FCSTD DOCUMENT  (FreeCAD 0.14R2935 (Git))
Label: C-beam gantry plate
License: CC-BY 3.0
LicenseURL: http://creativecommons.org/licenses/by/3.0/
objects: Mesh::Feature×1, Sketcher::SketchObject×1
note: 1 computed .brp shape members not serialized (recipe doc carries the construction recipe); baked Part::Feature solids carry a one-line shape summary decoded from their .brp

FEATURE [Mesh::Feature] C_Beam_Gantry_Plate_V1_STL  label="C-Beam_Gantry Plate_V1_STL"
FEATURE [Sketcher::SketchObject] Sketch
  Placement = pos=(77.6,0,0) rot=(0,0,1;1.5708rad)
  sketch-geometry (18):
    g0: LineSegment StartX=0 StartY=0 StartZ=0 EndX=77.51 EndY=0 EndZ=0
    g1: LineSegment StartX=77.51 StartY=0 StartZ=0 EndX=77.51 EndY=77.51 EndZ=0
    g2: LineSegment StartX=77.51 StartY=77.51 StartZ=0 EndX=0 EndY=77.51 EndZ=0
    g3: LineSegment StartX=0 StartY=77.51 StartZ=0 EndX=0 EndY=0 EndZ=0
    g4: Circle CenterX=8.75 CenterY=68.76 CenterZ=0 NormalX=0 NormalY=0 NormalZ=1 Radius=2.55
    g5: Circle CenterX=8.76 CenterY=38.76 CenterZ=0 NormalX=0 NormalY=0 NormalZ=1 Radius=2.55
    g6: Circle CenterX=8.76 CenterY=8.76 CenterZ=0 NormalX=0 NormalY=0 NormalZ=1 Radius=2.55
    g7: Circle CenterX=28.75 CenterY=68.75 CenterZ=0 NormalX=0 NormalY=0 NormalZ=1 Radius=2.55
    g8: Circle CenterX=48.75 CenterY=68.75 CenterZ=0 NormalX=0 NormalY=0 NormalZ=1 Radius=2.55
    g9: Circle CenterX=68.75 CenterY=68.75 CenterZ=0 NormalX=0 NormalY=0 NormalZ=1 Radius=2.55
    g10: Circle CenterX=68.75 CenterY=8.76 CenterZ=0 NormalX=0 NormalY=0 NormalZ=1 Radius=2.55
    g11: Circle CenterX=48.76 CenterY=8.76 CenterZ=0 NormalX=0 NormalY=0 NormalZ=1 Radius=2.55
    g12: Circle CenterX=28.76 CenterY=8.76 CenterZ=0 NormalX=0 NormalY=0 NormalZ=1 Radius=2.55
    g13: Circle CenterX=68.75 CenterY=38.76 CenterZ=0 NormalX=0 NormalY=0 NormalZ=1 Radius=2.55
    g14: Circle CenterX=18.755 CenterY=58.7909 CenterZ=0 NormalX=0 NormalY=0 NormalZ=1 Radius=2.55
    g15: Circle CenterX=58.755 CenterY=58.7765 CenterZ=0 NormalX=0 NormalY=0 NormalZ=1 Radius=2.53802
    g16: Circle CenterX=58.7985 CenterY=18.7777 CenterZ=0 NormalX=0 NormalY=0 NormalZ=1 Radius=2.49102
    g17: Circle CenterX=18.7993 CenterY=18.8618 CenterZ=0 NormalX=0 NormalY=0 NormalZ=1 Radius=2.47518
  constraints (45):
    c: Coincident(g0,g1)
    c: Coincident(g1,g2)
    c: Coincident(g2,g3)
    c: Coincident(g3,g0)
    c: Horizontal(g0)
    c: Horizontal(g2)
    c: Vertical(g1)
    c: Vertical(g3)
    c: Coincident(g0,g-1)
    c: DistanceY(g-1,g2) = 77.51
    c: DistanceX(g2,g1) = 77.51
    c: DistanceY(g4) = 68.76
    c: Radius(g4) = 2.55
    c: Radius(g5) = 2.55
    c: Radius(g6) = 2.55
    c: Radius(g7) = 2.55
    c: DistanceY(g-1,g6) = 8.76
    c: DistanceY(g-1,g5) = 38.76
    c: Radius(g8) = 2.55
    c: DistanceX(g-1,g6) = 8.76
    c: DistanceX(g-1,g5) = 8.76
    c: Distance(g4,g7) = 20
    c: Distance(g7,g8) = 20
    c: DistanceY(g7,g2) = 8.76
    c: DistanceY(g8,g1) = 8.76
    c: DistanceX(g9,g8) = -20
    c: Radius(g9) = 2.55
    c: DistanceY(g1,g9) = -8.76
    c: DistanceX(g1,g9) = -8.76
    c: Radius(g10) = 2.55
    c: DistanceY(g10,g0) = -8.76
    c: DistanceX(g10,g0) = 8.76
    c: Radius(g12) = 2.55
    c: Radius(g11) = 2.55
    c: DistanceY(g11,g0) = -8.76
    c: DistanceY(g12,g0) = -8.76
    c: DistanceX(g12,g6) = -20
    c: DistanceX(g12,g11) = 20
    c: DistanceX(g10) = 68.75
    c: Radius(g13) = 2.55
    c: DistanceY(g13,g0) = -38.76
    c: DistanceX(g13,g1) = 8.76
    c: Radius(g14) = 2.55
    c: DistanceX(g-2,g14) = 18.755
    c: DistanceX(g15,g14) = -40
